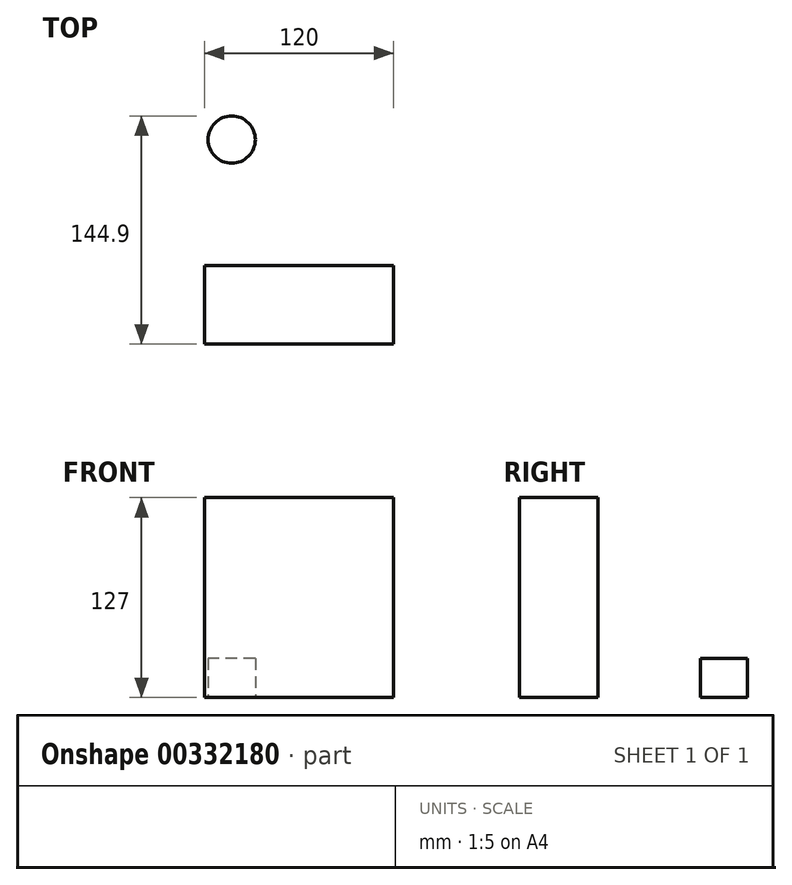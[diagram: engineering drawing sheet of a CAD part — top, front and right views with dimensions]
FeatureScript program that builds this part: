
annotation { "Feature Type Name" : "Feature", "Feature Type Description" : "" }
export const myFeature = defineFeature(function(context is Context, id is Id, definition is map)
    precondition{}
    {
        {
            var Q0;
            Q0=qCreatedBy(makeId("Top.planeOp"),FACE);
            var sketch = newSketch(context, id + "F0", { "sketchPlane" : qUnion([Q0])});
            skLineSegment(sketch, "E0.bottom", {"start": v(-57.18, -39.81) * mm, "end": v(62.82, -39.81) * mm});
            skLineSegment(sketch, "E0.top", {"start": v(-57.18, 10.19) * mm, "end": v(62.82, 10.19) * mm});
            skLineSegment(sketch, "E0.left", {"start": v(-57.18, -39.81) * mm, "end": v(-57.18, 10.19) * mm});
            skLineSegment(sketch, "E0.right", {"start": v(62.82, -39.81) * mm, "end": v(62.82, 10.19) * mm});
            skSolve(sketch);
        }
        {
            var Q0;
            Q0=makeQuery(id+"F0.imprint","IMPRINT",FACE,{"disambiguationData":[TD([[makeQuery(id+"F0.imprint","IMPRINT",EDGE,{"derivedFrom":sQuery(id+"F0.wireOp",EDGE,"E0.bottom")}),1.0]])]});
            extrude(context, id + "F1", {"entities" : qUnion([Q0]), "depth" : 127 * mm});
        }
        {
            var Q0;
            Q0=qCreatedBy(makeId("Top.planeOp"),FACE);
            var sketch = newSketch(context, id + "F2", { "sketchPlane" : qUnion([Q0])});
            skCircle(sketch, "E1", {"center": v(-39.94, 90.09) * mm, "radius": 15 * mm});
            skSolve(sketch);
        }
        {
            var Q0;
            Q0=makeQuery(id+"F2.imprint","IMPRINT",FACE,{"disambiguationData":[TD([[makeQuery(id+"F2.imprint","IMPRINT",EDGE,{"derivedFrom":sQuery(id+"F2.wireOp",EDGE,"E1")}),1.0]])]});
            extrude(context, id + "F3", {"entities" : qUnion([Q0]), "depth" : 25 * mm});
        }
    });
